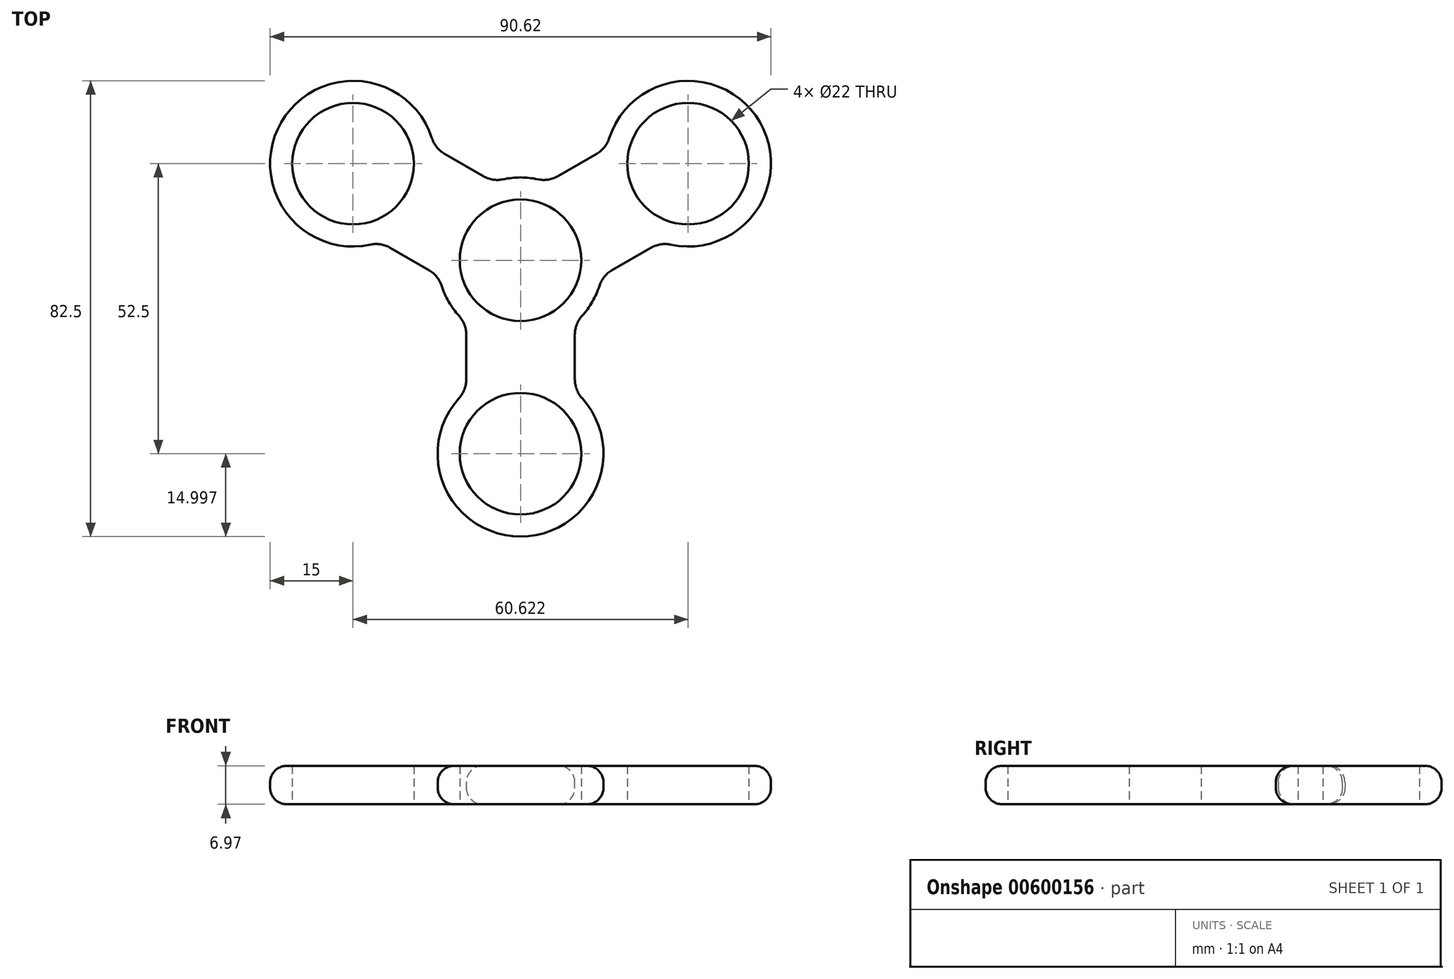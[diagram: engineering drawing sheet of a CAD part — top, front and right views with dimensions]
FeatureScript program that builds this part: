
annotation { "Feature Type Name" : "Feature", "Feature Type Description" : "" }
export const myFeature = defineFeature(function(context is Context, id is Id, definition is map)
    precondition{}
    {
        {
            var Q0;
            Q0=qCreatedBy(makeId("Top.planeOp"),FACE);
            var sketch = newSketch(context, id + "F0", { "sketchPlane" : qUnion([Q0])});
            skCircle(sketch, "E0", {"center": v(-117.85, 62.5) * mm, "radius": 15 * mm});
            skLineSegment(sketch, "E1", {"start": v(-117.85, 62.5) * mm, "end": v(-117.85, 27.5) * mm});
            skLineSegment(sketch, "E2", {"start": v(-117.85, 62.5) * mm, "end": v(-148.16, 80) * mm});
            skLineSegment(sketch, "E3", {"start": v(-117.85, 62.5) * mm, "end": v(-87.54, 80) * mm});
            skCircle(sketch, "E4", {"center": v(-117.85, 27.5) * mm, "radius": 15 * mm});
            skCircle(sketch, "E5", {"center": v(-148.16, 80) * mm, "radius": 15 * mm});
            skCircle(sketch, "E6", {"center": v(-87.54, 80) * mm, "radius": 15 * mm});
            skLineSegment(sketch, "E7.bottom", {"start": v(-108.02, 38.83) * mm, "end": v(-127.67, 38.83) * mm});
            skLineSegment(sketch, "E7.top", {"start": v(-108.02, 51.16) * mm, "end": v(-127.67, 51.16) * mm});
            skLineSegment(sketch, "E7.left", {"start": v(-108.02, 38.83) * mm, "end": v(-108.02, 51.16) * mm});
            skLineSegment(sketch, "E7.right", {"start": v(-127.67, 38.83) * mm, "end": v(-127.67, 51.16) * mm});
            skPoint(sketch, "E7.middle", {"position": v(-117.85, 45) * mm});
            skLineSegment(sketch, "E8.bottom", {"start": v(-133.43, 82.84) * mm, "end": v(-143.26, 65.82) * mm});
            skLineSegment(sketch, "E8.top", {"start": v(-122.75, 76.67) * mm, "end": v(-132.58, 59.66) * mm});
            skLineSegment(sketch, "E8.left", {"start": v(-133.43, 82.84) * mm, "end": v(-122.75, 76.67) * mm});
            skLineSegment(sketch, "E8.right", {"start": v(-143.26, 65.82) * mm, "end": v(-132.58, 59.66) * mm});
            skPoint(sketch, "E8.middle", {"position": v(-133, 71.25) * mm});
            skCircle(sketch, "E9", {"center": v(-87.54, 80) * mm, "radius": 11 * mm});
            skLineSegment(sketch, "E10.bottom", {"start": v(-92.44, 65.82) * mm, "end": v(-102.27, 82.84) * mm});
            skLineSegment(sketch, "E10.top", {"start": v(-103.12, 59.66) * mm, "end": v(-112.95, 76.67) * mm});
            skLineSegment(sketch, "E10.left", {"start": v(-92.44, 65.82) * mm, "end": v(-103.12, 59.66) * mm});
            skLineSegment(sketch, "E10.right", {"start": v(-102.27, 82.84) * mm, "end": v(-112.95, 76.67) * mm});
            skPoint(sketch, "E10.middle", {"position": v(-102.7, 71.25) * mm});
            skCircle(sketch, "E11", {"center": v(-117.85, 27.5) * mm, "radius": 11 * mm});
            skCircle(sketch, "E12", {"center": v(-148.16, 80) * mm, "radius": 11 * mm});
            skCircle(sketch, "E13", {"center": v(-117.85, 62.5) * mm, "radius": 11 * mm});
            skSolve(sketch);
        }
        {
            var Q0;
            Q0 = qSketchRegion(id + "F0", true);
            extrude(context, id + "F1", {"entities" : qUnion([Q0]), "depth" : 6.97 * mm, "offsetDistance" : 25 * mm});
        }
        {
            var Q0;
            Q0=makeQuery(id+"F1.opExtrude","SWEPT_EDGE",EDGE,{"disambiguationData":[OSD([sQuery(id+"F0.wireOp",EDGE,"E0"),sQuery(id+"F0.wireOp",EDGE,"E8.top"),sQuery(id+"F0.wireOp",EDGE,"E8.left")])]});
            var Q1;
            Q1=makeQuery(id+"F1.opExtrude","SWEPT_EDGE",EDGE,{"disambiguationData":[OSD([sQuery(id+"F0.wireOp",EDGE,"E0"),sQuery(id+"F0.wireOp",EDGE,"E10.top"),sQuery(id+"F0.wireOp",EDGE,"E10.right")])]});
            var Q2;
            Q2=makeQuery(id+"F1.opExtrude","SWEPT_EDGE",EDGE,{"disambiguationData":[OSD([sQuery(id+"F0.wireOp",EDGE,"E6"),sQuery(id+"F0.wireOp",EDGE,"E10.bottom"),sQuery(id+"F0.wireOp",EDGE,"E10.right")])]});
            var Q3;
            Q3=makeQuery(id+"F1.opExtrude","SWEPT_EDGE",EDGE,{"disambiguationData":[OSD([sQuery(id+"F0.wireOp",EDGE,"E5"),sQuery(id+"F0.wireOp",EDGE,"E8.bottom"),sQuery(id+"F0.wireOp",EDGE,"E8.left")])]});
            var Q4;
            Q4=makeQuery(id+"F1.opExtrude","SWEPT_EDGE",EDGE,{"disambiguationData":[OSD([sQuery(id+"F0.wireOp",EDGE,"E5"),sQuery(id+"F0.wireOp",EDGE,"E8.bottom"),sQuery(id+"F0.wireOp",EDGE,"E8.right")])]});
            var Q5;
            Q5=makeQuery(id+"F1.opExtrude","SWEPT_EDGE",EDGE,{"disambiguationData":[OSD([sQuery(id+"F0.wireOp",EDGE,"E0"),sQuery(id+"F0.wireOp",EDGE,"E8.top"),sQuery(id+"F0.wireOp",EDGE,"E8.right")])]});
            var Q6;
            Q6=makeQuery(id+"F1.opExtrude","SWEPT_EDGE",EDGE,{"disambiguationData":[OSD([sQuery(id+"F0.wireOp",EDGE,"E0"),sQuery(id+"F0.wireOp",EDGE,"E7.top"),sQuery(id+"F0.wireOp",EDGE,"E7.right")])]});
            var Q7;
            Q7=makeQuery(id+"F1.opExtrude","SWEPT_EDGE",EDGE,{"disambiguationData":[OSD([sQuery(id+"F0.wireOp",EDGE,"E4"),sQuery(id+"F0.wireOp",EDGE,"E7.bottom"),sQuery(id+"F0.wireOp",EDGE,"E7.right")])]});
            var Q8;
            Q8=makeQuery(id+"F1.opExtrude","SWEPT_EDGE",EDGE,{"disambiguationData":[OSD([sQuery(id+"F0.wireOp",EDGE,"E6"),sQuery(id+"F0.wireOp",EDGE,"E10.bottom"),sQuery(id+"F0.wireOp",EDGE,"E10.left")])]});
            var Q9;
            Q9=makeQuery(id+"F1.opExtrude","SWEPT_EDGE",EDGE,{"disambiguationData":[OSD([sQuery(id+"F0.wireOp",EDGE,"E0"),sQuery(id+"F0.wireOp",EDGE,"E10.top"),sQuery(id+"F0.wireOp",EDGE,"E10.left")])]});
            var Q10;
            Q10=makeQuery(id+"F1.opExtrude","SWEPT_EDGE",EDGE,{"disambiguationData":[OSD([sQuery(id+"F0.wireOp",EDGE,"E0"),sQuery(id+"F0.wireOp",EDGE,"E7.top"),sQuery(id+"F0.wireOp",EDGE,"E7.left")])]});
            var Q11;
            Q11=makeQuery(id+"F1.opExtrude","SWEPT_EDGE",EDGE,{"disambiguationData":[OSD([sQuery(id+"F0.wireOp",EDGE,"E4"),sQuery(id+"F0.wireOp",EDGE,"E7.bottom"),sQuery(id+"F0.wireOp",EDGE,"E7.left")])]});
            fillet(context, id + "F2", {"entities" : qUnion([Q0, Q1, Q2, Q3, Q4, Q5, Q6, Q7, Q8, Q9, Q10, Q11]), "radius" : 5 * mm, "tangentPropagation" : true, "allowEdgeOverflow" : false});
        }
        {
            var Q0;
            Q0=makeQuery(id+"F1.opExtrude","CAP_EDGE",EDGE,{"disambiguationData":[OSD([sQuery(id+"F0.wireOp",EDGE,"E8.right")])],"isStart":false});
            var Q1;
            {var subQ0=sQuery(id+"F0.wireOp",EDGE,"E0");Q1=makeQuery(id+"F1.opExtrude","CAP_EDGE",EDGE,{"disambiguationData":[OSD([subQ0]),TDD([makeQuery(id+"F0.imprint","IMPRINT",EDGE,{"disambiguationData":[TD([[makeQuery(id+"F0.imprint","INTERSECT",VERTEX,{"derivedFrom":[subQ0,sQuery(id+"F0.wireOp",EDGE,"E7.top"),sQuery(id+"F0.wireOp",EDGE,"E7.right")]}),1.0]])],"derivedFrom":subQ0})])],"isStart":true});}
            fillet(context, id + "F3", {"entities" : qUnion([Q0, Q1]), "radius" : 3 * mm, "tangentPropagation" : true, "allowEdgeOverflow" : false});
        }
    });
